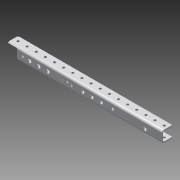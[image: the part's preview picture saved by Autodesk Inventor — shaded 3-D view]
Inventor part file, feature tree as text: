
AUTODESK INVENTOR PART (.ipt)
format: ipt  version: 2015 (Build 190159000, 159)  size: 310,784 bytes
history: native  units: in
note: dims shown in document units (in); Inventor stores cm internally (conversion verified against a paired STEP export)
features: projected_geometry x10, sketch x4, extrude x3, other x2, hole x1, imported_body x1
ambient origin geometry x8: Origin, YZ Plane, XZ Plane, XY Plane, X Axis, Y Axis, Z Axis, Center Point
bodies: Body1 (feature_tree)
feature tree (21):
  other  "Cut-Extrude6"
  other  "C-Channel 2.ipt1"
  extrude  "Extrusion1"  Depth=0.6875in
  hole  "Hole1"  [1 undecoded]
  extrude  "Extrusion2"  Depth=1.125in
  extrude  "Extrusion3"  Depth=1.125in
  imported_body  "Base1"
  sketch  "Sketch1"  dims[d0=13.0in d1=0.0in d2=0.6875in]
  projected_geometry  "Projected Loop1"
  projected_geometry  "Projected Loop2"
  projected_geometry  "Projected Loop3"
  projected_geometry  "Projected Loop4"
  projected_geometry  "Projected Loop5"
  projected_geometry  "Projected Loop6"
  sketch  "Sketch2"  dims[d3=0.6875in d4=1.625in]
  projected_geometry  "Projected Loop7"
  projected_geometry  "Projected Loop8"
  sketch  "Sketch3"  dims[d5=6.5in]
  projected_geometry  "Projected Loop9"
  sketch  "Sketch6"  dims[d6=0.25in d7=0.75in d8=0.375in d9=0.25in d10=0.5635in d11=1.0in d12=0.8108in d13=1.125in d14=1.125in d15=1.0in d16=0.0in d17=0.125in d18=0.0in]
  projected_geometry  "Projected Loop10"
note: 1 required parameter value undecoded (feature->parameter linkage not recoverable at this tier; creation-order binding heuristic only, values carry confidence <= 0.55)
